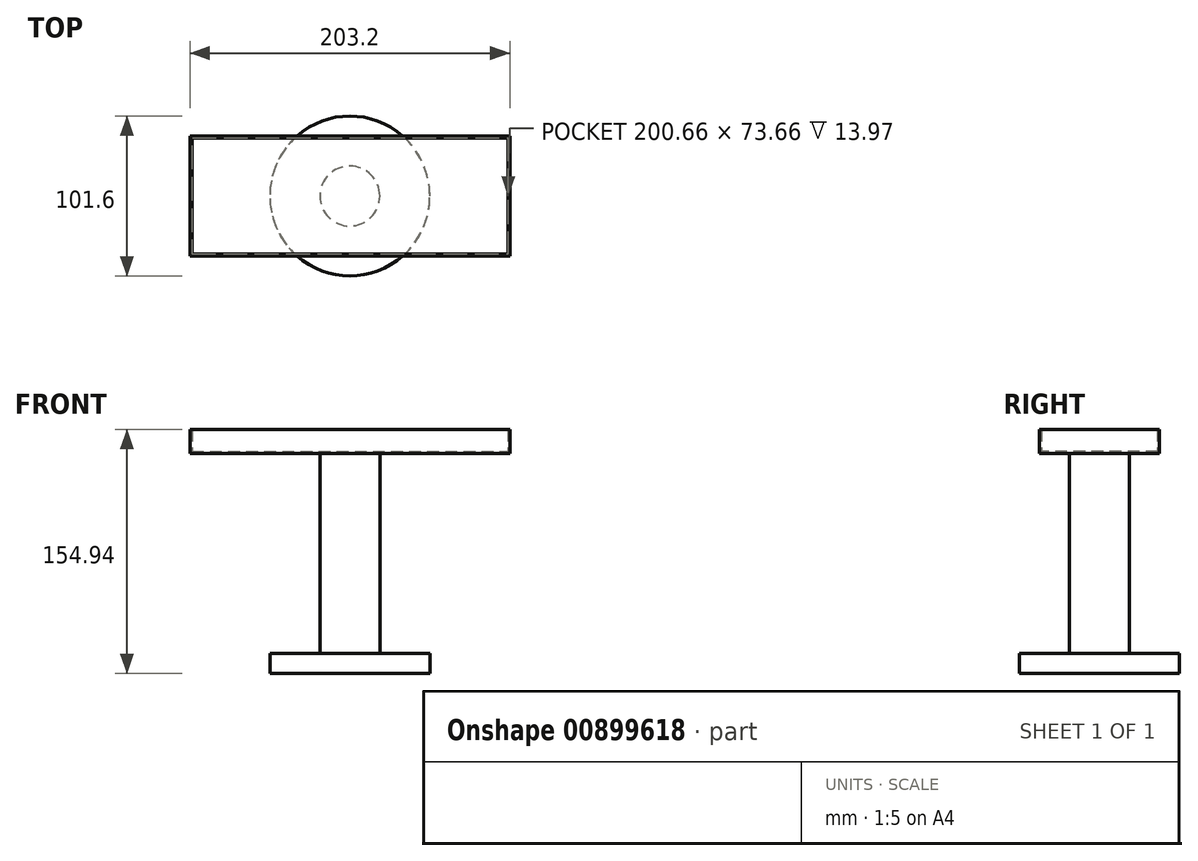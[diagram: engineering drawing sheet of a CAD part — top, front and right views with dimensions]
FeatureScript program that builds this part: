
annotation { "Feature Type Name" : "Feature", "Feature Type Description" : "" }
export const myFeature = defineFeature(function(context is Context, id is Id, definition is map)
    precondition{}
    {
        {
            var Q0;
            Q0=qCreatedBy(makeId("Top.planeOp"),FACE);
            var sketch = newSketch(context, id + "F0", { "sketchPlane" : qUnion([Q0])});
            skCircle(sketch, "E0", {"center": v(0, 0) * mm, "radius": 50.8 * mm});
            skSolve(sketch);
        }
        {
            var Q0;
            Q0=makeQuery(id+"F0.imprint","IMPRINT",FACE,{"disambiguationData":[TD([[makeQuery(id+"F0.imprint","IMPRINT",EDGE,{"derivedFrom":sQuery(id+"F0.wireOp",EDGE,"E0")}),1.0]])]});
            extrude(context, id + "F1", {"entities" : qUnion([Q0]), "depth" : 12.7 * mm, "offsetDistance" : 25.4 * mm});
        }
        {
            var Q0;
            Q0=makeQuery(id+"F1.opExtrude","CAP_FACE",FACE,{"disambiguationData":[OSD([sQuery(id+"F0.wireOp",EDGE,"E0")])],"isStart":false});
            var sketch = newSketch(context, id + "F2", { "sketchPlane" : qUnion([Q0])});
            skCircle(sketch, "E1", {"center": v(0, 0) * mm, "radius": 19.05 * mm});
            skSolve(sketch);
        }
        {
            var Q0;
            Q0=makeQuery(id+"F2.imprint","IMPRINT",FACE,{"disambiguationData":[TD([[makeQuery(id+"F2.imprint","IMPRINT",EDGE,{"derivedFrom":sQuery(id+"F2.wireOp",EDGE,"E1")}),1.0]])]});
            extrude(context, id + "F3", {"entities" : qUnion([Q0]), "operationType" : NewBodyOperationType.ADD, "depth" : 127 * mm, "offsetDistance" : 25.4 * mm});
        }
        {
            var Q0;
            Q0=makeQuery(id+"F3.opExtrude","CAP_FACE",FACE,{"disambiguationData":[OSD([sQuery(id+"F2.wireOp",EDGE,"E1")])],"isStart":false});
            var sketch = newSketch(context, id + "F4", { "sketchPlane" : qUnion([Q0])});
            skLineSegment(sketch, "E2.bottom", {"start": v(-101.6, 38.1) * mm, "end": v(101.6, 38.1) * mm});
            skLineSegment(sketch, "E2.top", {"start": v(-101.6, -38.1) * mm, "end": v(101.6, -38.1) * mm});
            skLineSegment(sketch, "E2.left", {"start": v(-101.6, 38.1) * mm, "end": v(-101.6, -38.1) * mm});
            skLineSegment(sketch, "E2.right", {"start": v(101.6, 38.1) * mm, "end": v(101.6, -38.1) * mm});
            skSolve(sketch);
        }
        {
            var Q0;
            Q0=makeQuery(id+"F4.imprint","IMPRINT",FACE,{"disambiguationData":[TD([[makeQuery(id+"F4.imprint","IMPRINT",EDGE,{"derivedFrom":sQuery(id+"F4.wireOp",EDGE,"E2.bottom")}),-1.0]])]});
            var Q1;
            Q1=makeQuery(id+"F4.imprint","IMPRINT",FACE,{"disambiguationData":[TD([[makeQuery(id+"F4.imprint","IMPRINT",EDGE,{"derivedFrom":makeQuery(id+"F3.opExtrude","CAP_EDGE",EDGE,{"disambiguationData":[OSD([sQuery(id+"F2.wireOp",EDGE,"E1")])],"isStart":false})}),1.0]])]});
            extrude(context, id + "F5", {"entities" : qUnion([Q0, Q1]), "depth" : 15.24 * mm, "offsetDistance" : 25.4 * mm});
        }
        {
            var Q0;
            Q0=makeQuery(id+"F5.opExtrude","CAP_FACE",FACE,{"disambiguationData":[OSD([sQuery(id+"F4.wireOp",EDGE,"E2.bottom"),sQuery(id+"F4.wireOp",EDGE,"E2.top"),sQuery(id+"F4.wireOp",EDGE,"E2.left"),sQuery(id+"F4.wireOp",EDGE,"E2.right")])],"isStart":false});
            shell(context, id + "F6", {"entities" : qUnion([Q0]), "thickness" : 1.27 * mm});
        }
    });
